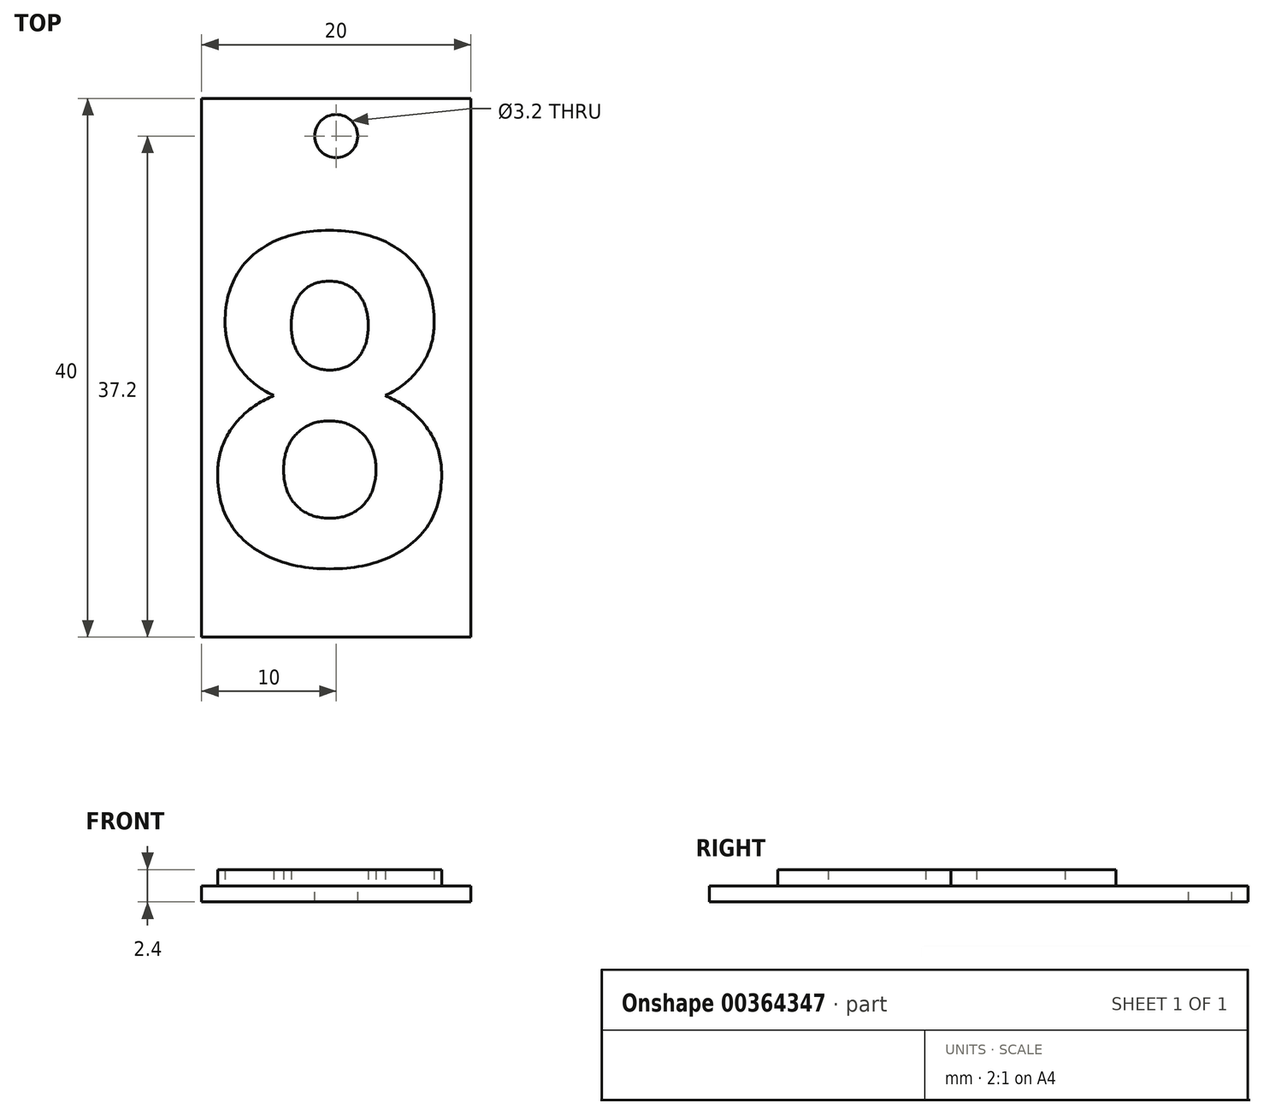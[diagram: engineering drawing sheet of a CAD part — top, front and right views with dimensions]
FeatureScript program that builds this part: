
annotation { "Feature Type Name" : "Feature", "Feature Type Description" : "" }
export const myFeature = defineFeature(function(context is Context, id is Id, definition is map)
    precondition{}
    {
        {
            var Q0;
            Q0=qCreatedBy(makeId("Top.planeOp"),FACE);
            var sketch = newSketch(context, id + "F0", { "sketchPlane" : qUnion([Q0])});
            skLineSegment(sketch, "E0.bottom", {"start": v(10, -20) * mm, "end": v(-10, -20) * mm});
            skLineSegment(sketch, "E0.top", {"start": v(10, 20) * mm, "end": v(-10, 20) * mm});
            skLineSegment(sketch, "E0.left", {"start": v(10, -20) * mm, "end": v(10, 20) * mm});
            skLineSegment(sketch, "E0.right", {"start": v(-10, -20) * mm, "end": v(-10, 20) * mm});
            skPoint(sketch, "E0.middle", {"position": v(0, 0) * mm});
            skCircle(sketch, "E1", {"center": v(0, 17.2) * mm, "radius": 1.6 * mm});
            skLineSegment(sketch, "E2", {"start": v(0, -20) * mm, "end": v(0, 15.6) * mm, "construction": true});
            skLineSegment(sketch, "E3", {"start": v(-10, -2.2) * mm, "end": v(10, -2.2) * mm, "construction": true});
            skPoint(sketch, "E3.startSnap0", {"position": v(0, -2.2) * mm});
            skLineSegment(sketch, "E4", {"start": v(10, -2.2) * mm, "end": v(-10, -2.2) * mm, "construction": true});
            skText(sketch, "E5", { "text": "8", "fontName": "RobotoSlab-Bold.ttf"});
            skLineSegment(sketch, "E6", {"start": v(-9.93, 10.17) * mm, "end": v(9.93, -14.57) * mm, "construction": true});
            skLineSegment(sketch, "E7", {"start": v(9.93, 10.17) * mm, "end": v(-9.93, -14.57) * mm, "construction": true});
            const initialGuessF0  = {"E5": [-0.00993, -0.01457, 1, 0, 0.02473]};
            skSetInitialGuess(sketch, initialGuessF0);
            skSolve(sketch);
        }
        {
            var Q0;
            Q0=makeQuery(id+"F0.imprint","IMPRINT",FACE,{"disambiguationData":[TD([[makeQuery(id+"F0.imprint","IMPRINT",EDGE,{"derivedFrom":sQuery(id+"F0.wireOp",EDGE,"E0.bottom")}),-1.0]])]});
            var Q1;
            Q1=makeQuery(id+"F0.imprint","IMPRINT",FACE,{"disambiguationData":[TD([[makeQuery(id+"F0.imprint","IMPRINT",EDGE,{"derivedFrom":sQuery(id+"F0.wireOp",EDGE,"E5.sketch_text.stroke-0")}),-1.0]])]});
            var Q2;
            Q2=makeQuery(id+"F0.imprint","IMPRINT",FACE,{"disambiguationData":[TD([[makeQuery(id+"F0.imprint","IMPRINT",EDGE,{"derivedFrom":sQuery(id+"F0.wireOp",EDGE,"E5.sketch_text.stroke-16")}),1.0]])]});
            var Q3;
            Q3=makeQuery(id+"F0.imprint","IMPRINT",FACE,{"disambiguationData":[TD([[makeQuery(id+"F0.imprint","IMPRINT",EDGE,{"derivedFrom":sQuery(id+"F0.wireOp",EDGE,"E5.sketch_text.stroke-24")}),1.0]])]});
            extrude(context, id + "F1", {"entities" : qUnion([Q0, Q1, Q2, Q3]), "oppositeDirection" : true, "depth" : 1.2 * mm});
        }
        {
            var Q0;
            Q0=makeQuery(id+"F0.imprint","IMPRINT",FACE,{"disambiguationData":[TD([[makeQuery(id+"F0.imprint","IMPRINT",EDGE,{"derivedFrom":sQuery(id+"F0.wireOp",EDGE,"E5.sketch_text.stroke-0")}),-1.0]])]});
            extrude(context, id + "F2", {"entities" : qUnion([Q0]), "operationType" : NewBodyOperationType.ADD, "depth" : 1.2 * mm});
        }
    });
